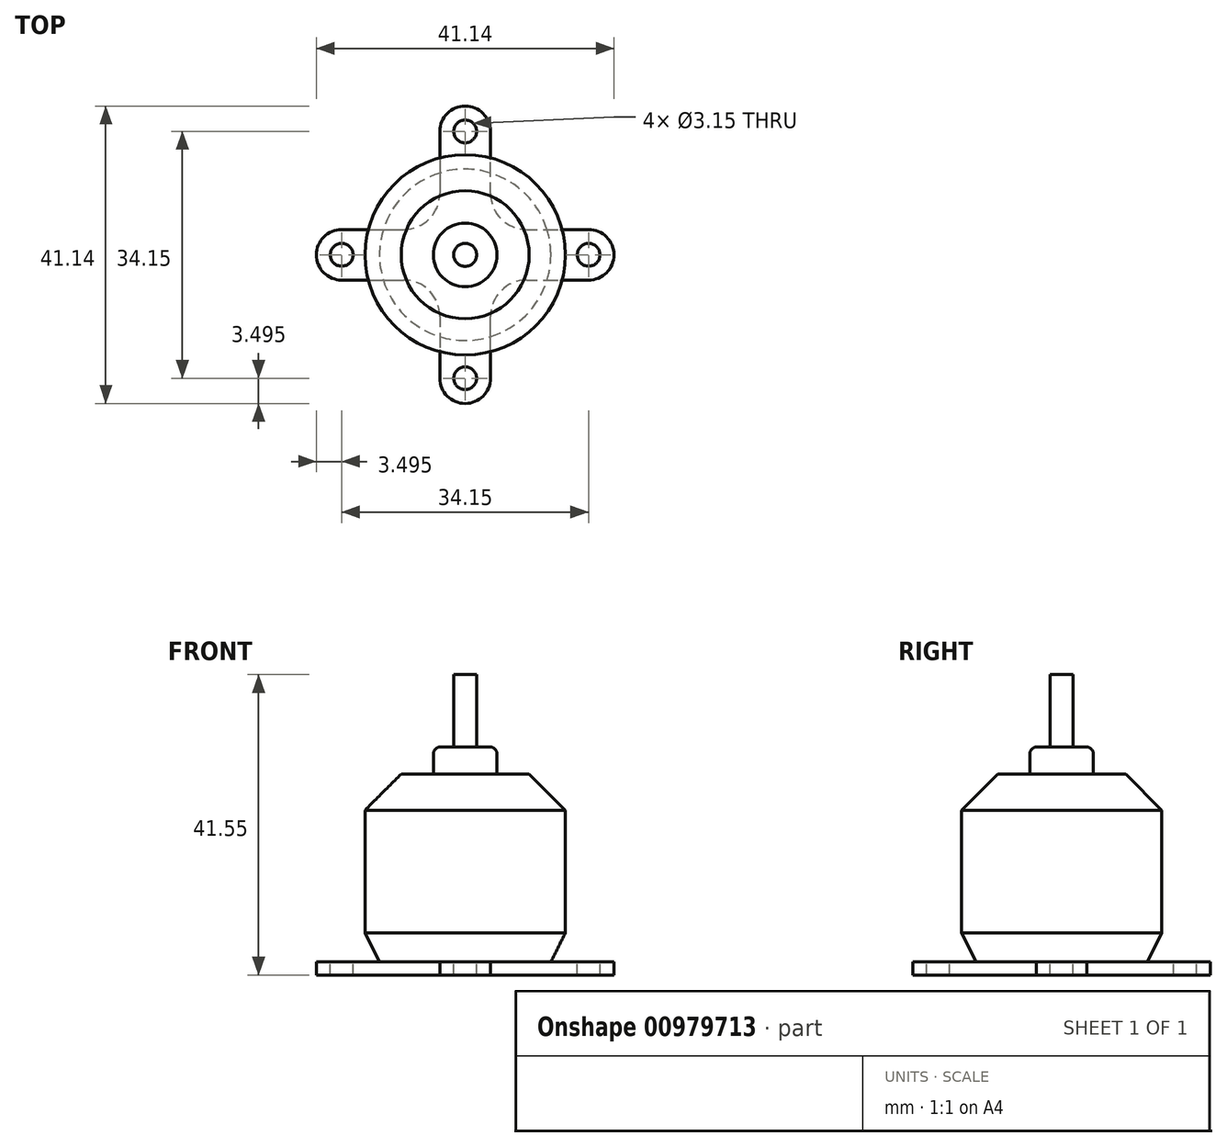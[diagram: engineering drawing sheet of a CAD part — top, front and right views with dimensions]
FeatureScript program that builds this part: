
annotation { "Feature Type Name" : "Feature", "Feature Type Description" : "" }
export const myFeature = defineFeature(function(context is Context, id is Id, definition is map)
    precondition{}
    {
        {
            var Q0;
            Q0=qCreatedBy(makeId("Front.planeOp"),FACE);
            var sketch = newSketch(context, id + "F0", { "sketchPlane" : qUnion([Q0])});
            skLineSegment(sketch, "E0.bottom", {"start": v(0, 0) * mm, "end": v(2.24, 0) * mm});
            skLineSegment(sketch, "E0.top", {"start": v(0, 41) * mm, "end": v(1.59, 41) * mm});
            skLineSegment(sketch, "E0.left", {"start": v(0, 0) * mm, "end": v(0, 41) * mm});
            skLineSegment(sketch, "E0.right", {"start": v(13.85, 1.25) * mm, "end": v(13.85, 27.25) * mm});
            skLineSegment(sketch, "E1", {"start": v(13.85, 1.25) * mm, "end": v(2.24, 1.25) * mm});
            skLineSegment(sketch, "E2", {"start": v(2.24, 1.25) * mm, "end": v(2.24, 0) * mm});
            skLineSegment(sketch, "E3", {"start": v(1.59, 41) * mm, "end": v(1.59, 31) * mm});
            skLineSegment(sketch, "E4", {"start": v(1.59, 31) * mm, "end": v(4.4, 31) * mm});
            skLineSegment(sketch, "E5", {"start": v(4.4, 31) * mm, "end": v(4.4, 27.25) * mm});
            skLineSegment(sketch, "E6", {"start": v(4.4, 27.25) * mm, "end": v(13.85, 27.25) * mm});
            skPoint(sketch, "E7.orphan", {"position": v(13.85, 0) * mm});
            skLineSegment(sketch, "E8", {"start": v(0, 51.67) * mm, "end": v(0, 56.1) * mm, "construction": true});
            skSolve(sketch);
        }
        {
            var Q0;
            Q0 = qSketchRegion(id + "F0", true);
            var Q1;
            Q1=sQuery(id+"F0.wireOp",EDGE,"E8");
            revolve(context, id + "F1", {"surfaceOperationType" : NewSurfaceOperationType.NEW, "entities" : qUnion([Q0]), "axis" : qUnion([Q1]), "revolveType" : RevolveType.FULL});
        }
        {
            var Q0;
            Q0=makeQuery(id+"F1.opRevolve","SWEPT_EDGE",EDGE,{"disambiguationData":[OSD([sQuery(id+"F0.wireOp",EDGE,"E0.right"),sQuery(id+"F0.wireOp",EDGE,"E6")])]});
            chamfer(context, id + "F2", {"entities" : qUnion([Q0]), "width" : 5 * mm, "tangentPropagation" : true});
        }
        {
            var Q0;
            Q0=makeQuery(id+"F1.opRevolve","SWEPT_EDGE",EDGE,{"disambiguationData":[OSD([sQuery(id+"F0.wireOp",EDGE,"E0.right"),sQuery(id+"F0.wireOp",EDGE,"E1")])]});
            chamfer(context, id + "F3", {"entities" : qUnion([Q0]), "chamferType" : ChamferType.TWO_OFFSETS, "width1" : 2 * mm, "oppositeDirection" : false, "width2" : 4 * mm, "tangentPropagation" : true});
        }
        {
            var Q0;
            Q0=makeQuery(id+"F1.opRevolve","SWEPT_EDGE",EDGE,{"disambiguationData":[OSD([sQuery(id+"F0.wireOp",EDGE,"E4"),sQuery(id+"F0.wireOp",EDGE,"E5")])]});
            fillet(context, id + "F4", {"entities" : qUnion([Q0]), "tangentPropagation" : true, "radius" : 1 * mm, "defaultsChanged" : true, "vertexSettings" : [], "allowEdgeOverflow" : false});
        }
        {
            var Q0;
            Q0=makeQuery(id+"F1.opRevolve","SWEPT_FACE",FACE,{"disambiguationData":[OSD([sQuery(id+"F0.wireOp",EDGE,"E1")])]});
            var sketch = newSketch(context, id + "F5", { "sketchPlane" : qUnion([Q0])});
            skLineSegment(sketch, "E9", {"start": v(-17.07, 0) * mm, "end": v(17.07, 0) * mm, "construction": true});
            skLineSegment(sketch, "E10", {"start": v(0, -17.07) * mm, "end": v(0, 17.07) * mm, "construction": true});
            skArc(sketch, "E11", {"start": v(-17.07, 3.5) * mm, "mid": v(-20.57, 0) * mm, "end": v(-17.07, -3.5) * mm});
            skCircle(sketch, "E12", {"center": v(-17.07, 0) * mm, "radius": 1.57 * mm});
            skArc(sketch, "E13", {"start": v(3.5, 17.07) * mm, "mid": v(0, 20.57) * mm, "end": v(-3.5, 17.07) * mm});
            skCircle(sketch, "E14", {"center": v(0, 17.07) * mm, "radius": 1.57 * mm});
            skCircle(sketch, "E15", {"center": v(17.07, 0) * mm, "radius": 1.57 * mm});
            skArc(sketch, "E16", {"start": v(17.07, -3.5) * mm, "mid": v(20.57, 0) * mm, "end": v(17.07, 3.5) * mm});
            skCircle(sketch, "E17", {"center": v(0, -17.07) * mm, "radius": 1.57 * mm});
            skArc(sketch, "E18", {"start": v(-3.5, -17.07) * mm, "mid": v(0, -20.57) * mm, "end": v(3.5, -17.07) * mm});
            skLineSegment(sketch, "E19", {"start": v(3.5, 17.07) * mm, "end": v(3.5, 3.5) * mm});
            skLineSegment(sketch, "E20", {"start": v(-3.5, -17.07) * mm, "end": v(-3.5, -3.5) * mm});
            skLineSegment(sketch, "E21", {"start": v(-17.07, 3.5) * mm, "end": v(-3.5, 3.5) * mm});
            skLineSegment(sketch, "E22", {"start": v(-17.07, -3.5) * mm, "end": v(-3.5, -3.5) * mm});
            skLineSegment(sketch, "E23.trimOffspring", {"start": v(3.5, 3.5) * mm, "end": v(17.07, 3.5) * mm});
            skLineSegment(sketch, "E24.trimOffspring", {"start": v(3.5, -3.5) * mm, "end": v(3.5, -17.07) * mm});
            skLineSegment(sketch, "E25.trimOffspring", {"start": v(3.5, -3.5) * mm, "end": v(17.07, -3.5) * mm});
            skLineSegment(sketch, "E26.trimOffspring", {"start": v(-3.5, 3.5) * mm, "end": v(-3.5, 17.07) * mm});
            skSolve(sketch);
        }
        {
            var Q0;
            Q0 = qSketchRegion(id + "F5", true);
            extrude(context, id + "F6", {"entities" : qUnion([Q0]), "operationType" : NewBodyOperationType.ADD, "depth" : 1.8 * mm, "offsetDistance" : 25 * mm});
        }
        {
            var Q0;
            Q0=makeQuery(id+"F6.opExtrude","SWEPT_EDGE",EDGE,{"disambiguationData":[OSD([sQuery(id+"F5.wireOp",EDGE,"E21"),sQuery(id+"F5.wireOp",EDGE,"E26.trimOffspring")])]});
            var Q1;
            Q1=makeQuery(id+"F6.opExtrude","SWEPT_EDGE",EDGE,{"disambiguationData":[OSD([sQuery(id+"F5.wireOp",EDGE,"E20"),sQuery(id+"F5.wireOp",EDGE,"E22")])]});
            var Q2;
            Q2=makeQuery(id+"F6.opExtrude","SWEPT_EDGE",EDGE,{"disambiguationData":[OSD([sQuery(id+"F5.wireOp",EDGE,"E24.trimOffspring"),sQuery(id+"F5.wireOp",EDGE,"E25.trimOffspring")])]});
            var Q3;
            Q3=makeQuery(id+"F6.opExtrude","SWEPT_EDGE",EDGE,{"disambiguationData":[OSD([sQuery(id+"F5.wireOp",EDGE,"E19"),sQuery(id+"F5.wireOp",EDGE,"E23.trimOffspring")])]});
            fillet(context, id + "F7", {"entities" : qUnion([Q0, Q1, Q2, Q3]), "tangentPropagation" : true, "radius" : 5 * mm, "defaultsChanged" : false, "vertexSettings" : [], "allowEdgeOverflow" : false});
        }
    });
